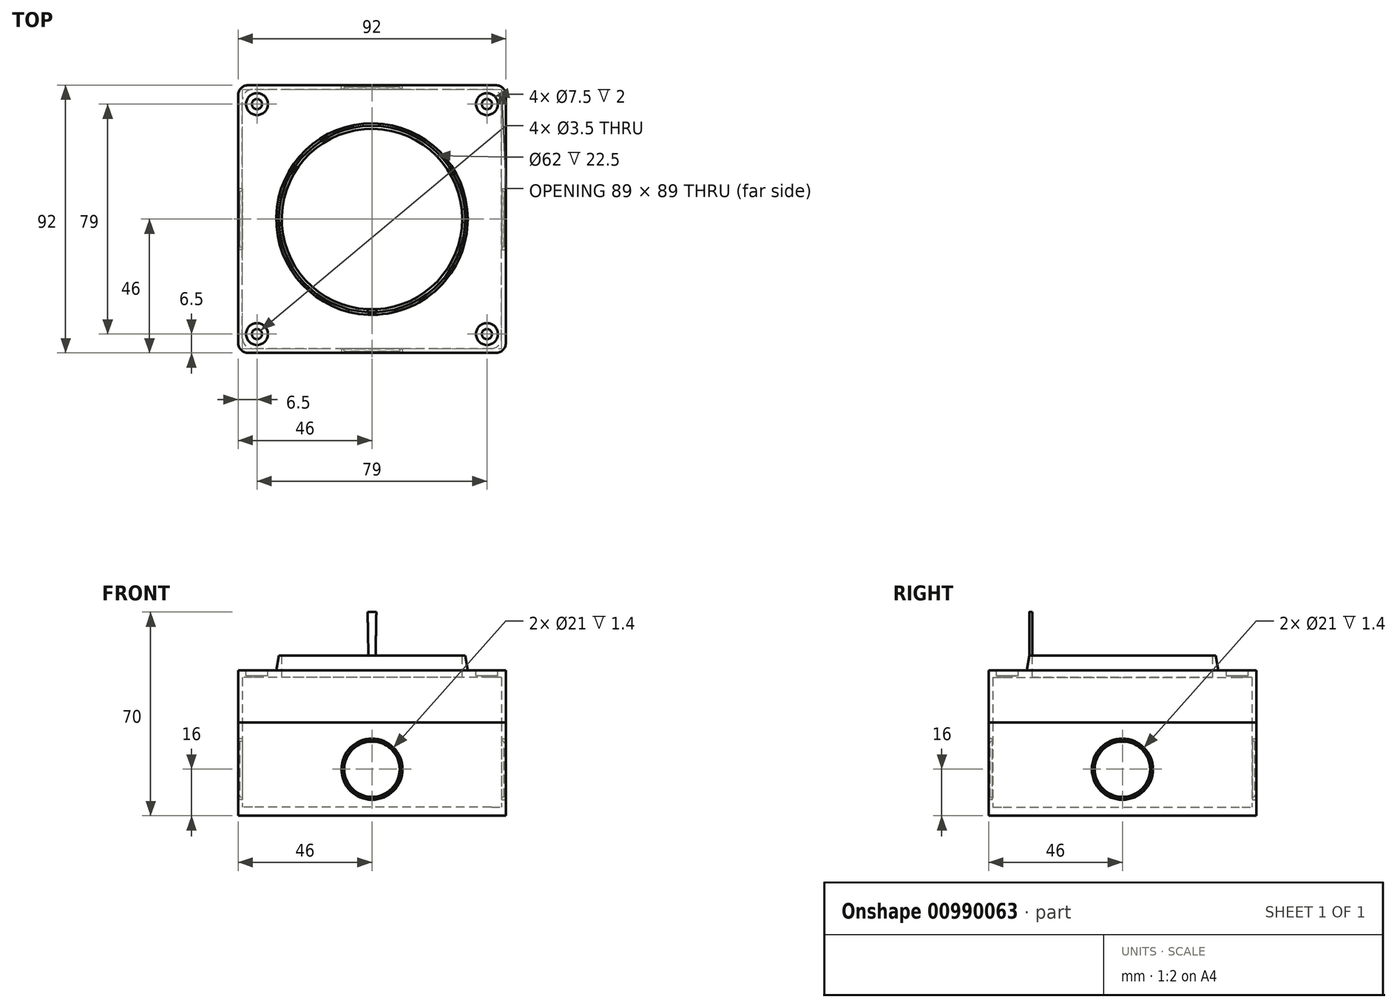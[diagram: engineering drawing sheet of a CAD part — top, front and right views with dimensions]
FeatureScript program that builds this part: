
annotation { "Feature Type Name" : "Feature", "Feature Type Description" : "" }
export const myFeature = defineFeature(function(context is Context, id is Id, definition is map)
    precondition{}
    {
        {
            var Q0;
            Q0=qCreatedBy(makeId("Top.planeOp"),FACE);
            var sketch = newSketch(context, id + "F0", { "sketchPlane" : qUnion([Q0])});
            skLineSegment(sketch, "E0.bottom", {"start": v(46, -46) * mm, "end": v(-46, -46) * mm});
            skLineSegment(sketch, "E0.top", {"start": v(46, 46) * mm, "end": v(-46, 46) * mm});
            skLineSegment(sketch, "E0.left", {"start": v(46, -46) * mm, "end": v(46, 46) * mm});
            skLineSegment(sketch, "E0.right", {"start": v(-46, -46) * mm, "end": v(-46, 46) * mm});
            skPoint(sketch, "E0.middle", {"position": v(0, 0) * mm});
            skSolve(sketch);
        }
        {
            var Q0;
            Q0=makeQuery(id+"F0.imprint","IMPRINT",FACE,{"disambiguationData":[TD([[makeQuery(id+"F0.imprint","IMPRINT",EDGE,{"derivedFrom":sQuery(id+"F0.wireOp",EDGE,"E0.bottom")}),-1.0]])]});
            extrude(context, id + "F1", {"entities" : qUnion([Q0]), "depth" : 3 * mm, "offsetDistance" : 25 * mm});
        }
        {
            var Q0;
            Q0=makeQuery(id+"F1.opExtrude","SWEPT_EDGE",EDGE,{"disambiguationData":[OSD([sQuery(id+"F0.wireOp",EDGE,"E0.bottom"),sQuery(id+"F0.wireOp",EDGE,"E0.right")])]});
            var Q1;
            Q1=makeQuery(id+"F1.opExtrude","SWEPT_EDGE",EDGE,{"disambiguationData":[OSD([sQuery(id+"F0.wireOp",EDGE,"E0.bottom"),sQuery(id+"F0.wireOp",EDGE,"E0.left")])]});
            var Q2;
            Q2=makeQuery(id+"F1.opExtrude","SWEPT_EDGE",EDGE,{"disambiguationData":[OSD([sQuery(id+"F0.wireOp",EDGE,"E0.top"),sQuery(id+"F0.wireOp",EDGE,"E0.left")])]});
            var Q3;
            Q3=makeQuery(id+"F1.opExtrude","SWEPT_EDGE",EDGE,{"disambiguationData":[OSD([sQuery(id+"F0.wireOp",EDGE,"E0.top"),sQuery(id+"F0.wireOp",EDGE,"E0.right")])]});
            fillet(context, id + "F2", {"entities" : qUnion([Q0, Q1, Q2, Q3]), "radius" : 3.5 * mm, "tangentPropagation" : true, "allowEdgeOverflow" : false});
        }
        {
            var Q0;
            Q0=makeQuery(id+"F1.opExtrude","CAP_FACE",FACE,{"disambiguationData":[OSD([sQuery(id+"F0.wireOp",EDGE,"E0.bottom"),sQuery(id+"F0.wireOp",EDGE,"E0.top"),sQuery(id+"F0.wireOp",EDGE,"E0.left"),sQuery(id+"F0.wireOp",EDGE,"E0.right")])],"isStart":false});
            cPlane(context, id + "F3", {"entities" : qUnion([Q0]), "cplaneType" : CPlaneType.OFFSET, "offset" : 0 * mm, "width" : 150 * mm, "height" : 150 * mm});
        }
        {
            var Q0;
            Q0=qCreatedBy(id+"F3.planeOp",FACE);
            var sketch = newSketch(context, id + "F4", { "sketchPlane" : qUnion([Q0])});
            skLineSegment(sketch, "E1.bottom", {"start": v(46, -46) * mm, "end": v(-46, -46) * mm});
            skLineSegment(sketch, "E1.top", {"start": v(46, 46) * mm, "end": v(-46, 46) * mm});
            skLineSegment(sketch, "E1.left", {"start": v(46, -46) * mm, "end": v(46, 46) * mm});
            skLineSegment(sketch, "E1.right", {"start": v(-46, -46) * mm, "end": v(-46, 46) * mm});
            skPoint(sketch, "E1.middle", {"position": v(0, 0) * mm});
            skLineSegment(sketch, "E2.bottom", {"start": v(44.5, -44.5) * mm, "end": v(-44.5, -44.5) * mm});
            skLineSegment(sketch, "E2.top", {"start": v(44.5, 44.5) * mm, "end": v(-44.5, 44.5) * mm});
            skLineSegment(sketch, "E2.left", {"start": v(44.5, -44.5) * mm, "end": v(44.5, 44.5) * mm});
            skLineSegment(sketch, "E2.right", {"start": v(-44.5, -44.5) * mm, "end": v(-44.5, 44.5) * mm});
            skSolve(sketch);
        }
        {
            var Q0;
            Q0 = qSketchRegion(id + "F4", true);
            extrude(context, id + "F5", {"entities" : qUnion([Q0]), "operationType" : NewBodyOperationType.ADD, "depth" : 29 * mm, "offsetDistance" : 25 * mm});
        }
        {
            var Q0;
            Q0=makeQuery(id+"F5.opExtrude","SWEPT_EDGE",EDGE,{"disambiguationData":[OSD([sQuery(id+"F4.wireOp",EDGE,"E2.bottom"),sQuery(id+"F4.wireOp",EDGE,"E2.right")])]});
            var Q1;
            Q1=makeQuery(id+"F5.opExtrude","SWEPT_EDGE",EDGE,{"disambiguationData":[OSD([sQuery(id+"F4.wireOp",EDGE,"E1.bottom"),sQuery(id+"F4.wireOp",EDGE,"E1.right")])]});
            var Q2;
            Q2=makeQuery(id+"F5.opExtrude","SWEPT_EDGE",EDGE,{"disambiguationData":[OSD([sQuery(id+"F4.wireOp",EDGE,"E1.top"),sQuery(id+"F4.wireOp",EDGE,"E1.right")])]});
            var Q3;
            Q3=makeQuery(id+"F5.opExtrude","SWEPT_EDGE",EDGE,{"disambiguationData":[OSD([sQuery(id+"F4.wireOp",EDGE,"E2.top"),sQuery(id+"F4.wireOp",EDGE,"E2.right")])]});
            var Q4;
            Q4=makeQuery(id+"F5.opExtrude","SWEPT_EDGE",EDGE,{"disambiguationData":[OSD([sQuery(id+"F4.wireOp",EDGE,"E1.top"),sQuery(id+"F4.wireOp",EDGE,"E1.left")])]});
            var Q5;
            Q5=makeQuery(id+"F5.opExtrude","SWEPT_EDGE",EDGE,{"disambiguationData":[OSD([sQuery(id+"F4.wireOp",EDGE,"E2.top"),sQuery(id+"F4.wireOp",EDGE,"E2.left")])]});
            var Q6;
            Q6=makeQuery(id+"F5.opExtrude","SWEPT_EDGE",EDGE,{"disambiguationData":[OSD([sQuery(id+"F4.wireOp",EDGE,"E1.bottom"),sQuery(id+"F4.wireOp",EDGE,"E1.left")])]});
            var Q7;
            Q7=makeQuery(id+"F5.opExtrude","SWEPT_EDGE",EDGE,{"disambiguationData":[OSD([sQuery(id+"F4.wireOp",EDGE,"E2.bottom"),sQuery(id+"F4.wireOp",EDGE,"E2.left")])]});
            fillet(context, id + "F6", {"entities" : qUnion([Q0, Q1, Q2, Q3, Q4, Q5, Q6, Q7]), "radius" : 3.5 * mm, "tangentPropagation" : true, "allowEdgeOverflow" : false});
        }
        {
            var Q0;
            Q0=makeQuery(id+"F5.boolean.opBoolean","MERGE",FACE,{"derivedFrom":[makeQuery(id+"F1.opExtrude","SWEPT_FACE",FACE,{"disambiguationData":[OSD([sQuery(id+"F0.wireOp",EDGE,"E0.bottom")])]}),makeQuery(id+"F5.opExtrude","SWEPT_FACE",FACE,{"disambiguationData":[OSD([sQuery(id+"F4.wireOp",EDGE,"E1.bottom")])]})]});
            var sketch = newSketch(context, id + "F7", { "sketchPlane" : qUnion([Q0])});
            skPoint(sketch, "E3", {"position": v(0, 16) * mm});
            skCircle(sketch, "E4", {"center": v(0, 16) * mm, "radius": 10.5 * mm});
            skSolve(sketch);
        }
        {
            var Q0;
            Q0=makeQuery(id+"F7.imprint","IMPRINT",FACE,{"disambiguationData":[TD([[makeQuery(id+"F7.imprint","IMPRINT",EDGE,{"derivedFrom":sQuery(id+"F7.wireOp",EDGE,"E4")}),1.0]])]});
            extrude(context, id + "F8", {"entities" : qUnion([Q0]), "operationType" : NewBodyOperationType.REMOVE, "oppositeDirection" : true, "depth" : 1.4 * mm, "offsetDistance" : 25 * mm});
        }
        {
            var Q0;
            Q0=makeQuery(id+"F8.boolean.opBoolean","COPY",FACE,{"derivedFrom":makeQuery(id+"F8.opExtrude","CAP_FACE",FACE,{"disambiguationData":[OSD([sQuery(id+"F7.wireOp",EDGE,"E4")])],"isStart":false})});
            var sketch = newSketch(context, id + "F9", { "sketchPlane" : qUnion([Q0])});
            skPoint(sketch, "E5", {"position": v(0, 16) * mm});
            skCircle(sketch, "E6", {"center": v(0, 16) * mm, "radius": 10 * mm});
            skSolve(sketch);
        }
        {
            var Q0;
            Q0=makeQuery(id+"F9.imprint","IMPRINT",FACE,{"disambiguationData":[TD([[makeQuery(id+"F9.imprint","IMPRINT",EDGE,{"derivedFrom":sQuery(id+"F9.wireOp",EDGE,"E6")}),1.0]])]});
            extrude(context, id + "F10", {"entities" : qUnion([Q0]), "operationType" : NewBodyOperationType.ADD, "depth" : 0.8 * mm, "offsetDistance" : 25 * mm});
        }
        {
            var Q0;
            Q0=makeQuery(id+"F10.opExtrude","CAP_EDGE",EDGE,{"disambiguationData":[OSD([sQuery(id+"F9.wireOp",EDGE,"E6")])],"isStart":false});
            chamfer(context, id + "F11", {"entities" : qUnion([Q0]), "chamferType" : ChamferType.OFFSET_ANGLE, "width" : 0.5 * mm, "oppositeDirection" : false, "angle" : 70 * degree});
        }
        {
            var Q0;
            Q0=makeQuery(id+"F5.boolean.opBoolean","MERGE",FACE,{"derivedFrom":[makeQuery(id+"F1.opExtrude","SWEPT_FACE",FACE,{"disambiguationData":[OSD([sQuery(id+"F0.wireOp",EDGE,"E0.right")])]}),makeQuery(id+"F5.opExtrude","SWEPT_FACE",FACE,{"disambiguationData":[OSD([sQuery(id+"F4.wireOp",EDGE,"E1.right")])]})]});
            var sketch = newSketch(context, id + "F12", { "sketchPlane" : qUnion([Q0])});
            skPoint(sketch, "E7", {"position": v(0, 16) * mm});
            skCircle(sketch, "E8", {"center": v(0, 16) * mm, "radius": 10.5 * mm});
            skSolve(sketch);
        }
        {
            var Q0;
            Q0=makeQuery(id+"F12.imprint","IMPRINT",FACE,{"disambiguationData":[TD([[makeQuery(id+"F12.imprint","IMPRINT",EDGE,{"derivedFrom":sQuery(id+"F12.wireOp",EDGE,"E8")}),1.0]])]});
            extrude(context, id + "F13", {"entities" : qUnion([Q0]), "operationType" : NewBodyOperationType.REMOVE, "oppositeDirection" : true, "depth" : 1.4 * mm, "offsetDistance" : 25 * mm});
        }
        {
            var Q0;
            Q0=makeQuery(id+"F13.boolean.opBoolean","COPY",FACE,{"derivedFrom":makeQuery(id+"F13.opExtrude","CAP_FACE",FACE,{"disambiguationData":[OSD([sQuery(id+"F12.wireOp",EDGE,"E8")])],"isStart":false})});
            var sketch = newSketch(context, id + "F14", { "sketchPlane" : qUnion([Q0])});
            skPoint(sketch, "E9", {"position": v(0, 16) * mm});
            skCircle(sketch, "E10", {"center": v(0, 16) * mm, "radius": 10 * mm});
            skSolve(sketch);
        }
        {
            var Q0;
            Q0=makeQuery(id+"F14.imprint","IMPRINT",FACE,{"disambiguationData":[TD([[makeQuery(id+"F14.imprint","IMPRINT",EDGE,{"derivedFrom":sQuery(id+"F14.wireOp",EDGE,"E10")}),1.0]])]});
            extrude(context, id + "F15", {"entities" : qUnion([Q0]), "operationType" : NewBodyOperationType.ADD, "depth" : 0.8 * mm, "offsetDistance" : 25 * mm});
        }
        {
            var Q0;
            Q0=makeQuery(id+"F15.opExtrude","CAP_EDGE",EDGE,{"disambiguationData":[OSD([sQuery(id+"F14.wireOp",EDGE,"E10")])],"isStart":false});
            chamfer(context, id + "F16", {"entities" : qUnion([Q0]), "chamferType" : ChamferType.OFFSET_ANGLE, "width" : 0.5 * mm, "oppositeDirection" : false, "angle" : 70 * degree, "tangentPropagation" : true});
        }
        {
            var Q0;
            Q0=makeQuery(id+"F5.boolean.opBoolean","MERGE",FACE,{"derivedFrom":[makeQuery(id+"F1.opExtrude","SWEPT_FACE",FACE,{"disambiguationData":[OSD([sQuery(id+"F0.wireOp",EDGE,"E0.top")])]}),makeQuery(id+"F5.opExtrude","SWEPT_FACE",FACE,{"disambiguationData":[OSD([sQuery(id+"F4.wireOp",EDGE,"E1.top")])]})]});
            var sketch = newSketch(context, id + "F17", { "sketchPlane" : qUnion([Q0])});
            skPoint(sketch, "E11", {"position": v(0, 16) * mm});
            skCircle(sketch, "E12", {"center": v(0, 16) * mm, "radius": 10.5 * mm});
            skSolve(sketch);
        }
        {
            var Q0;
            Q0=makeQuery(id+"F17.imprint","IMPRINT",FACE,{"disambiguationData":[TD([[makeQuery(id+"F17.imprint","IMPRINT",EDGE,{"derivedFrom":sQuery(id+"F17.wireOp",EDGE,"E12")}),1.0]])]});
            extrude(context, id + "F18", {"entities" : qUnion([Q0]), "operationType" : NewBodyOperationType.REMOVE, "oppositeDirection" : true, "depth" : 1.4 * mm, "offsetDistance" : 25 * mm});
        }
        {
            var Q0;
            Q0=makeQuery(id+"F18.boolean.opBoolean","COPY",FACE,{"derivedFrom":makeQuery(id+"F18.opExtrude","CAP_FACE",FACE,{"disambiguationData":[OSD([sQuery(id+"F17.wireOp",EDGE,"E12")])],"isStart":false})});
            var sketch = newSketch(context, id + "F19", { "sketchPlane" : qUnion([Q0])});
            skPoint(sketch, "E13", {"position": v(0, 16) * mm});
            skCircle(sketch, "E14", {"center": v(0, 16) * mm, "radius": 10 * mm});
            skSolve(sketch);
        }
        {
            var Q0;
            Q0=makeQuery(id+"F19.imprint","IMPRINT",FACE,{"disambiguationData":[TD([[makeQuery(id+"F19.imprint","IMPRINT",EDGE,{"derivedFrom":sQuery(id+"F19.wireOp",EDGE,"E14")}),1.0]])]});
            extrude(context, id + "F20", {"entities" : qUnion([Q0]), "operationType" : NewBodyOperationType.ADD, "depth" : 0.8 * mm, "offsetDistance" : 25 * mm});
        }
        {
            var Q0;
            Q0=makeQuery(id+"F20.opExtrude","CAP_EDGE",EDGE,{"disambiguationData":[OSD([sQuery(id+"F19.wireOp",EDGE,"E14")])],"isStart":false});
            chamfer(context, id + "F21", {"entities" : qUnion([Q0]), "chamferType" : ChamferType.OFFSET_ANGLE, "width" : 0.5 * mm, "oppositeDirection" : false, "angle" : 70 * degree, "tangentPropagation" : true});
        }
        {
            var Q0;
            Q0=makeQuery(id+"F5.boolean.opBoolean","MERGE",FACE,{"derivedFrom":[makeQuery(id+"F1.opExtrude","SWEPT_FACE",FACE,{"disambiguationData":[OSD([sQuery(id+"F0.wireOp",EDGE,"E0.left")])]}),makeQuery(id+"F5.opExtrude","SWEPT_FACE",FACE,{"disambiguationData":[OSD([sQuery(id+"F4.wireOp",EDGE,"E1.left")])]})]});
            var sketch = newSketch(context, id + "F22", { "sketchPlane" : qUnion([Q0])});
            skPoint(sketch, "E15", {"position": v(0, 16) * mm});
            skCircle(sketch, "E16", {"center": v(0, 16) * mm, "radius": 10.5 * mm});
            skSolve(sketch);
        }
        {
            var Q0;
            Q0=makeQuery(id+"F22.imprint","IMPRINT",FACE,{"disambiguationData":[TD([[makeQuery(id+"F22.imprint","IMPRINT",EDGE,{"derivedFrom":sQuery(id+"F22.wireOp",EDGE,"E16")}),1.0]])]});
            extrude(context, id + "F23", {"entities" : qUnion([Q0]), "operationType" : NewBodyOperationType.REMOVE, "oppositeDirection" : true, "depth" : 1.4 * mm, "offsetDistance" : 25 * mm});
        }
        {
            var Q0;
            Q0=makeQuery(id+"F23.boolean.opBoolean","COPY",FACE,{"derivedFrom":makeQuery(id+"F23.opExtrude","CAP_FACE",FACE,{"disambiguationData":[OSD([sQuery(id+"F22.wireOp",EDGE,"E16")])],"isStart":false})});
            var sketch = newSketch(context, id + "F24", { "sketchPlane" : qUnion([Q0])});
            skPoint(sketch, "E17", {"position": v(0, 16) * mm});
            skCircle(sketch, "E18", {"center": v(0, 16) * mm, "radius": 10 * mm});
            skSolve(sketch);
        }
        {
            var Q0;
            Q0=makeQuery(id+"F24.imprint","IMPRINT",FACE,{"disambiguationData":[TD([[makeQuery(id+"F24.imprint","IMPRINT",EDGE,{"derivedFrom":sQuery(id+"F24.wireOp",EDGE,"E18")}),1.0]])]});
            extrude(context, id + "F25", {"entities" : qUnion([Q0]), "operationType" : NewBodyOperationType.ADD, "depth" : 0.8 * mm, "offsetDistance" : 25 * mm});
        }
        {
            var Q0;
            Q0=makeQuery(id+"F25.opExtrude","CAP_EDGE",EDGE,{"disambiguationData":[OSD([sQuery(id+"F24.wireOp",EDGE,"E18")])],"isStart":false});
            chamfer(context, id + "F26", {"entities" : qUnion([Q0]), "chamferType" : ChamferType.OFFSET_ANGLE, "width" : 0.5 * mm, "oppositeDirection" : false, "angle" : 70 * degree, "tangentPropagation" : true});
        }
        {
            var Q0;
            Q0=makeQuery(id+"F5.opExtrude","CAP_FACE",FACE,{"disambiguationData":[OSD([sQuery(id+"F4.wireOp",EDGE,"E1.bottom"),sQuery(id+"F4.wireOp",EDGE,"E1.top"),sQuery(id+"F4.wireOp",EDGE,"E1.left"),sQuery(id+"F4.wireOp",EDGE,"E1.right"),sQuery(id+"F4.wireOp",EDGE,"E2.bottom"),sQuery(id+"F4.wireOp",EDGE,"E2.top"),sQuery(id+"F4.wireOp",EDGE,"E2.left"),sQuery(id+"F4.wireOp",EDGE,"E2.right")])],"isStart":false});
            cPlane(context, id + "F27", {"entities" : qUnion([Q0]), "cplaneType" : CPlaneType.OFFSET, "offset" : 0 * mm, "width" : 150 * mm, "height" : 150 * mm});
        }
        {
            var Q0;
            Q0=qCreatedBy(id+"F27.planeOp",FACE);
            var sketch = newSketch(context, id + "F28", { "sketchPlane" : qUnion([Q0])});
            skLineSegment(sketch, "E19.bottom", {"start": v(46, -46) * mm, "end": v(-46, -46) * mm});
            skLineSegment(sketch, "E19.top", {"start": v(46, 46) * mm, "end": v(-46, 46) * mm});
            skLineSegment(sketch, "E19.left", {"start": v(46, -46) * mm, "end": v(46, 46) * mm});
            skLineSegment(sketch, "E19.right", {"start": v(-46, -46) * mm, "end": v(-46, 46) * mm});
            skPoint(sketch, "E19.middle", {"position": v(0, 0) * mm});
            skLineSegment(sketch, "E20.bottom", {"start": v(44.5, -44.5) * mm, "end": v(-44.5, -44.5) * mm});
            skLineSegment(sketch, "E20.top", {"start": v(44.5, 44.5) * mm, "end": v(-44.5, 44.5) * mm});
            skLineSegment(sketch, "E20.left", {"start": v(44.5, -44.5) * mm, "end": v(44.5, 44.5) * mm});
            skLineSegment(sketch, "E20.right", {"start": v(-44.5, -44.5) * mm, "end": v(-44.5, 44.5) * mm});
            skSolve(sketch);
        }
        {
            var Q0;
            Q0 = qSketchRegion(id + "F28", true);
            extrude(context, id + "F29", {"entities" : qUnion([Q0]), "depth" : 15.5 * mm, "offsetDistance" : 25 * mm});
        }
        {
            var Q0;
            Q0=makeQuery(id+"F29.opExtrude","CAP_FACE",FACE,{"disambiguationData":[OSD([sQuery(id+"F28.wireOp",EDGE,"E19.bottom"),sQuery(id+"F28.wireOp",EDGE,"E19.top"),sQuery(id+"F28.wireOp",EDGE,"E19.left"),sQuery(id+"F28.wireOp",EDGE,"E19.right"),sQuery(id+"F28.wireOp",EDGE,"E20.bottom"),sQuery(id+"F28.wireOp",EDGE,"E20.top"),sQuery(id+"F28.wireOp",EDGE,"E20.left"),sQuery(id+"F28.wireOp",EDGE,"E20.right")])],"isStart":false});
            var sketch = newSketch(context, id + "F30", { "sketchPlane" : qUnion([Q0])});
            skLineSegment(sketch, "E21.bottom", {"start": v(46, -46) * mm, "end": v(-46, -46) * mm});
            skLineSegment(sketch, "E21.top", {"start": v(46, 46) * mm, "end": v(-46, 46) * mm});
            skLineSegment(sketch, "E21.left", {"start": v(46, -46) * mm, "end": v(46, 46) * mm});
            skLineSegment(sketch, "E21.right", {"start": v(-46, -46) * mm, "end": v(-46, 46) * mm});
            skPoint(sketch, "E21.middle", {"position": v(0, 0) * mm});
            skSolve(sketch);
        }
        {
            var Q0;
            Q0 = qSketchRegion(id + "F30", true);
            extrude(context, id + "F31", {"entities" : qUnion([Q0]), "operationType" : NewBodyOperationType.ADD, "depth" : 2.5 * mm, "offsetDistance" : 25 * mm});
        }
        {
            var Q0;
            Q0=makeQuery(id+"F31.boolean.opBoolean","MERGE",EDGE,{"derivedFrom":[makeQuery(id+"F29.opExtrude","SWEPT_EDGE",EDGE,{"disambiguationData":[OSD([sQuery(id+"F28.wireOp",EDGE,"E19.bottom"),sQuery(id+"F28.wireOp",EDGE,"E19.right")])]}),makeQuery(id+"F31.opExtrude","SWEPT_EDGE",EDGE,{"disambiguationData":[OSD([sQuery(id+"F30.wireOp",EDGE,"E21.bottom"),sQuery(id+"F30.wireOp",EDGE,"E21.right")])]})]});
            var Q1;
            Q1=makeQuery(id+"F29.opExtrude","SWEPT_EDGE",EDGE,{"disambiguationData":[OSD([sQuery(id+"F28.wireOp",EDGE,"E20.bottom"),sQuery(id+"F28.wireOp",EDGE,"E20.right")])]});
            var Q2;
            Q2=makeQuery(id+"F31.boolean.opBoolean","MERGE",EDGE,{"derivedFrom":[makeQuery(id+"F29.opExtrude","SWEPT_EDGE",EDGE,{"disambiguationData":[OSD([sQuery(id+"F28.wireOp",EDGE,"E19.bottom"),sQuery(id+"F28.wireOp",EDGE,"E19.left")])]}),makeQuery(id+"F31.opExtrude","SWEPT_EDGE",EDGE,{"disambiguationData":[OSD([sQuery(id+"F30.wireOp",EDGE,"E21.bottom"),sQuery(id+"F30.wireOp",EDGE,"E21.left")])]})]});
            var Q3;
            Q3=makeQuery(id+"F29.opExtrude","SWEPT_EDGE",EDGE,{"disambiguationData":[OSD([sQuery(id+"F28.wireOp",EDGE,"E20.bottom"),sQuery(id+"F28.wireOp",EDGE,"E20.left")])]});
            var Q4;
            Q4=makeQuery(id+"F29.opExtrude","SWEPT_EDGE",EDGE,{"disambiguationData":[OSD([sQuery(id+"F28.wireOp",EDGE,"E20.top"),sQuery(id+"F28.wireOp",EDGE,"E20.left")])]});
            var Q5;
            Q5=makeQuery(id+"F31.boolean.opBoolean","MERGE",EDGE,{"derivedFrom":[makeQuery(id+"F29.opExtrude","SWEPT_EDGE",EDGE,{"disambiguationData":[OSD([sQuery(id+"F28.wireOp",EDGE,"E19.top"),sQuery(id+"F28.wireOp",EDGE,"E19.left")])]}),makeQuery(id+"F31.opExtrude","SWEPT_EDGE",EDGE,{"disambiguationData":[OSD([sQuery(id+"F30.wireOp",EDGE,"E21.top"),sQuery(id+"F30.wireOp",EDGE,"E21.left")])]})]});
            var Q6;
            Q6=makeQuery(id+"F31.boolean.opBoolean","MERGE",EDGE,{"derivedFrom":[makeQuery(id+"F29.opExtrude","SWEPT_EDGE",EDGE,{"disambiguationData":[OSD([sQuery(id+"F28.wireOp",EDGE,"E19.top"),sQuery(id+"F28.wireOp",EDGE,"E19.right")])]}),makeQuery(id+"F31.opExtrude","SWEPT_EDGE",EDGE,{"disambiguationData":[OSD([sQuery(id+"F30.wireOp",EDGE,"E21.top"),sQuery(id+"F30.wireOp",EDGE,"E21.right")])]})]});
            var Q7;
            Q7=makeQuery(id+"F29.opExtrude","SWEPT_EDGE",EDGE,{"disambiguationData":[OSD([sQuery(id+"F28.wireOp",EDGE,"E20.top"),sQuery(id+"F28.wireOp",EDGE,"E20.right")])]});
            fillet(context, id + "F32", {"entities" : qUnion([Q0, Q1, Q2, Q3, Q4, Q5, Q6, Q7]), "radius" : 3.5 * mm, "tangentPropagation" : true, "allowEdgeOverflow" : false});
        }
        {
            var Q0;
            Q0=makeQuery(id+"F31.opExtrude","CAP_FACE",FACE,{"disambiguationData":[OSD([sQuery(id+"F30.wireOp",EDGE,"E21.bottom"),sQuery(id+"F30.wireOp",EDGE,"E21.top"),sQuery(id+"F30.wireOp",EDGE,"E21.left"),sQuery(id+"F30.wireOp",EDGE,"E21.right")])],"isStart":false});
            var sketch = newSketch(context, id + "F33", { "sketchPlane" : qUnion([Q0])});
            skPoint(sketch, "E22", {"position": v(39.5, -39.5) * mm});
            skPoint(sketch, "E23", {"position": v(-39.5, -39.5) * mm});
            skPoint(sketch, "E24", {"position": v(-39.5, 39.5) * mm});
            skPoint(sketch, "E25", {"position": v(39.5, 39.5) * mm});
            skLineSegment(sketch, "E26", {"start": v(39.5, 39.5) * mm, "end": v(39.5, 46) * mm, "construction": true});
            skLineSegment(sketch, "E27", {"start": v(39.5, 39.5) * mm, "end": v(46, 39.5) * mm, "construction": true});
            skCircle(sketch, "E28", {"center": v(39.5, 39.5) * mm, "radius": 3.75 * mm});
            skLineSegment(sketch, "E29", {"start": v(-39.5, 46) * mm, "end": v(-39.5, 39.5) * mm, "construction": true});
            skLineSegment(sketch, "E30", {"start": v(-39.5, 39.5) * mm, "end": v(-46, 39.5) * mm, "construction": true});
            skCircle(sketch, "E31", {"center": v(-39.5, 39.5) * mm, "radius": 3.75 * mm});
            skLineSegment(sketch, "E32", {"start": v(-39.5, -39.5) * mm, "end": v(-46, -39.5) * mm, "construction": true});
            skLineSegment(sketch, "E33", {"start": v(-39.5, -39.5) * mm, "end": v(-39.5, -46) * mm, "construction": true});
            skLineSegment(sketch, "E34", {"start": v(39.5, -39.5) * mm, "end": v(39.5, -46) * mm, "construction": true});
            skLineSegment(sketch, "E35", {"start": v(39.5, -39.5) * mm, "end": v(46, -39.5) * mm, "construction": true});
            skCircle(sketch, "E36", {"center": v(39.5, -39.5) * mm, "radius": 3.75 * mm});
            skCircle(sketch, "E37", {"center": v(-39.5, -39.5) * mm, "radius": 3.75 * mm});
            skSolve(sketch);
        }
        {
            var Q0;
            Q0=makeQuery(id+"F33.imprint","IMPRINT",FACE,{"disambiguationData":[TD([[makeQuery(id+"F33.imprint","IMPRINT",EDGE,{"derivedFrom":sQuery(id+"F33.wireOp",EDGE,"E31")}),1.0]])]});
            var Q1;
            Q1=makeQuery(id+"F33.imprint","IMPRINT",FACE,{"disambiguationData":[TD([[makeQuery(id+"F33.imprint","IMPRINT",EDGE,{"derivedFrom":sQuery(id+"F33.wireOp",EDGE,"E28")}),1.0]])]});
            var Q2;
            Q2=makeQuery(id+"F33.imprint","IMPRINT",FACE,{"disambiguationData":[TD([[makeQuery(id+"F33.imprint","IMPRINT",EDGE,{"derivedFrom":sQuery(id+"F33.wireOp",EDGE,"E36")}),1.0]])]});
            var Q3;
            Q3=makeQuery(id+"F33.imprint","IMPRINT",FACE,{"disambiguationData":[TD([[makeQuery(id+"F33.imprint","IMPRINT",EDGE,{"derivedFrom":sQuery(id+"F33.wireOp",EDGE,"E37")}),1.0]])]});
            extrude(context, id + "F34", {"entities" : qUnion([Q0, Q1, Q2, Q3]), "operationType" : NewBodyOperationType.REMOVE, "oppositeDirection" : true, "depth" : 2 * mm, "offsetDistance" : 25 * mm});
        }
        {
            var Q0;
            Q0=makeQuery(id+"F34.boolean.opBoolean","COPY",FACE,{"derivedFrom":makeQuery(id+"F34.opExtrude","CAP_FACE",FACE,{"disambiguationData":[OSD([sQuery(id+"F33.wireOp",EDGE,"E31")])],"isStart":false})});
            var sketch = newSketch(context, id + "F35", { "sketchPlane" : qUnion([Q0])});
            skPoint(sketch, "E38", {"position": v(-39.5, 39.5) * mm});
            skCircle(sketch, "E39", {"center": v(-39.5, 39.5) * mm, "radius": 1.75 * mm});
            skSolve(sketch);
        }
        {
            var Q0;
            Q0 = qSketchRegion(id + "F35", true);
            extrude(context, id + "F36", {"entities" : qUnion([Q0]), "operationType" : NewBodyOperationType.REMOVE, "oppositeDirection" : true, "depth" : 2.5 * mm, "offsetDistance" : 25 * mm});
        }
        {
            var Q0;
            Q0=makeQuery(id+"F34.boolean.opBoolean","COPY",FACE,{"derivedFrom":makeQuery(id+"F34.opExtrude","CAP_FACE",FACE,{"disambiguationData":[OSD([sQuery(id+"F33.wireOp",EDGE,"E28")])],"isStart":false})});
            var sketch = newSketch(context, id + "F37", { "sketchPlane" : qUnion([Q0])});
            skPoint(sketch, "E40", {"position": v(39.5, 39.5) * mm});
            skCircle(sketch, "E41", {"center": v(39.5, 39.5) * mm, "radius": 1.75 * mm});
            skSolve(sketch);
        }
        {
            var Q0;
            Q0 = qSketchRegion(id + "F37", true);
            extrude(context, id + "F38", {"entities" : qUnion([Q0]), "operationType" : NewBodyOperationType.REMOVE, "oppositeDirection" : true, "depth" : 2.5 * mm, "offsetDistance" : 25 * mm});
        }
        {
            var Q0;
            Q0=makeQuery(id+"F34.boolean.opBoolean","COPY",FACE,{"derivedFrom":makeQuery(id+"F34.opExtrude","CAP_FACE",FACE,{"disambiguationData":[OSD([sQuery(id+"F33.wireOp",EDGE,"E36")])],"isStart":false})});
            var sketch = newSketch(context, id + "F39", { "sketchPlane" : qUnion([Q0])});
            skPoint(sketch, "E42", {"position": v(39.5, -39.5) * mm});
            skCircle(sketch, "E43", {"center": v(39.5, -39.5) * mm, "radius": 1.75 * mm});
            skSolve(sketch);
        }
        {
            var Q0;
            Q0 = qSketchRegion(id + "F39", true);
            extrude(context, id + "F40", {"entities" : qUnion([Q0]), "operationType" : NewBodyOperationType.REMOVE, "oppositeDirection" : true, "depth" : 25 * mm, "offsetDistance" : 25 * mm});
        }
        {
            var Q0;
            Q0=makeQuery(id+"F34.boolean.opBoolean","COPY",FACE,{"derivedFrom":makeQuery(id+"F34.opExtrude","CAP_FACE",FACE,{"disambiguationData":[OSD([sQuery(id+"F33.wireOp",EDGE,"E37")])],"isStart":false})});
            var sketch = newSketch(context, id + "F41", { "sketchPlane" : qUnion([Q0])});
            skPoint(sketch, "E44", {"position": v(-39.5, -39.5) * mm});
            skCircle(sketch, "E45", {"center": v(-39.5, -39.5) * mm, "radius": 1.75 * mm});
            skSolve(sketch);
        }
        {
            var Q0;
            Q0 = qSketchRegion(id + "F41", true);
            extrude(context, id + "F42", {"entities" : qUnion([Q0]), "operationType" : NewBodyOperationType.REMOVE, "oppositeDirection" : true, "depth" : 25 * mm, "offsetDistance" : 25 * mm});
        }
        {
            var Q0;
            Q0=makeQuery(id+"F31.opExtrude","CAP_FACE",FACE,{"disambiguationData":[OSD([sQuery(id+"F30.wireOp",EDGE,"E21.bottom"),sQuery(id+"F30.wireOp",EDGE,"E21.top"),sQuery(id+"F30.wireOp",EDGE,"E21.left"),sQuery(id+"F30.wireOp",EDGE,"E21.right")])],"isStart":false});
            var sketch = newSketch(context, id + "F43", { "sketchPlane" : qUnion([Q0])});
            skPoint(sketch, "E46", {"position": v(0, 0) * mm});
            skCircle(sketch, "E47", {"center": v(0, 0) * mm, "radius": 33 * mm});
            skSolve(sketch);
        }
        {
            var Q0;
            Q0 = qSketchRegion(id + "F43", true);
            extrude(context, id + "F44", {"entities" : qUnion([Q0]), "operationType" : NewBodyOperationType.ADD, "depth" : 5 * mm, "offsetDistance" : 25 * mm});
        }
        {
            var Q0;
            Q0=makeQuery(id+"F44.opExtrude","CAP_EDGE",EDGE,{"disambiguationData":[OSD([sQuery(id+"F43.wireOp",EDGE,"E47")])],"isStart":false});
            chamfer(context, id + "F45", {"entities" : qUnion([Q0]), "chamferType" : ChamferType.OFFSET_ANGLE, "width" : 1 * mm, "oppositeDirection" : false, "angle" : 80 * degree});
        }
        {
            var Q0;
            Q0=makeQuery(id+"F44.opExtrude","CAP_FACE",FACE,{"disambiguationData":[OSD([sQuery(id+"F43.wireOp",EDGE,"E47")])],"isStart":false});
            var sketch = newSketch(context, id + "F46", { "sketchPlane" : qUnion([Q0])});
            skPoint(sketch, "E48", {"position": v(0, 0) * mm});
            skCircle(sketch, "E49", {"center": v(0, 0) * mm, "radius": 32 * mm});
            skSolve(sketch);
        }
        {
            var Q0;
            Q0 = qSketchRegion(id + "F46", true);
            extrude(context, id + "F47", {"entities" : qUnion([Q0]), "operationType" : NewBodyOperationType.ADD, "depth" : 15 * mm, "offsetDistance" : 25 * mm});
        }
        {
            var Q0;
            Q0=makeQuery(id+"F47.opExtrude","CAP_FACE",FACE,{"disambiguationData":[OSD([sQuery(id+"F46.wireOp",EDGE,"E49")])],"isStart":false});
            var sketch = newSketch(context, id + "F48", { "sketchPlane" : qUnion([Q0])});
            skPoint(sketch, "E50", {"position": v(0, 0) * mm});
            skCircle(sketch, "E51", {"center": v(0, 0) * mm, "radius": 31 * mm});
            skSolve(sketch);
        }
        {
            var Q0;
            Q0=makeQuery(id+"F48.imprint","IMPRINT",FACE,{"disambiguationData":[TD([[makeQuery(id+"F48.imprint","IMPRINT",EDGE,{"derivedFrom":sQuery(id+"F48.wireOp",EDGE,"E51")}),1.0]])]});
            extrude(context, id + "F49", {"entities" : qUnion([Q0]), "operationType" : NewBodyOperationType.REMOVE, "oppositeDirection" : true, "depth" : 25 * mm, "offsetDistance" : 25 * mm});
        }
        {
            var Q0;
            Q0=makeQuery(id+"F47.opExtrude","CAP_FACE",FACE,{"disambiguationData":[OSD([sQuery(id+"F46.wireOp",EDGE,"E49")])],"isStart":false});
            var sketch = newSketch(context, id + "F50", { "sketchPlane" : qUnion([Q0])});
            skPoint(sketch, "E52", {"position": v(0, -32) * mm});
            skPoint(sketch, "E53", {"position": v(32, 0) * mm});
            skPoint(sketch, "E54", {"position": v(0, 32) * mm});
            skPoint(sketch, "E55", {"position": v(-32, 0) * mm});
            skLineSegment(sketch, "E56", {"start": v(0, -32) * mm, "end": v(1.5, -31.96) * mm});
            skLineSegment(sketch, "E57", {"start": v(0, -32) * mm, "end": v(-1.5, -31.96) * mm});
            skPoint(sketch, "E58", {"position": v(0, -31) * mm});
            skLineSegment(sketch, "E59", {"start": v(0, -31) * mm, "end": v(1.5, -30.96) * mm});
            skLineSegment(sketch, "E60", {"start": v(0, -31) * mm, "end": v(-1.5, -30.96) * mm});
            skLineSegment(sketch, "E61", {"start": v(1.5, -30.96) * mm, "end": v(1.5, -31.96) * mm});
            skLineSegment(sketch, "E62", {"start": v(-1.5, -31.96) * mm, "end": v(-1.5, -30.96) * mm});
            skSolve(sketch);
        }
        {
            var Q0;
            {var subQ0=sQuery(id+"F50.wireOp",EDGE,"E61");Q0=makeQuery(id+"F50.imprint","IMPRINT",FACE,{"disambiguationData":[TD([[makeQuery(id+"F50.imprint","IMPRINT",EDGE,{"derivedFrom":subQ0}),1.0]])]});}
            extrude(context, id + "F51", {"entities" : qUnion([Q0]), "operationType" : NewBodyOperationType.REMOVE, "oppositeDirection" : true, "depth" : 15 * mm, "offsetDistance" : 25 * mm, "hasDraft" : true, "draftAngle" : 1 * degree});
        }
    });
